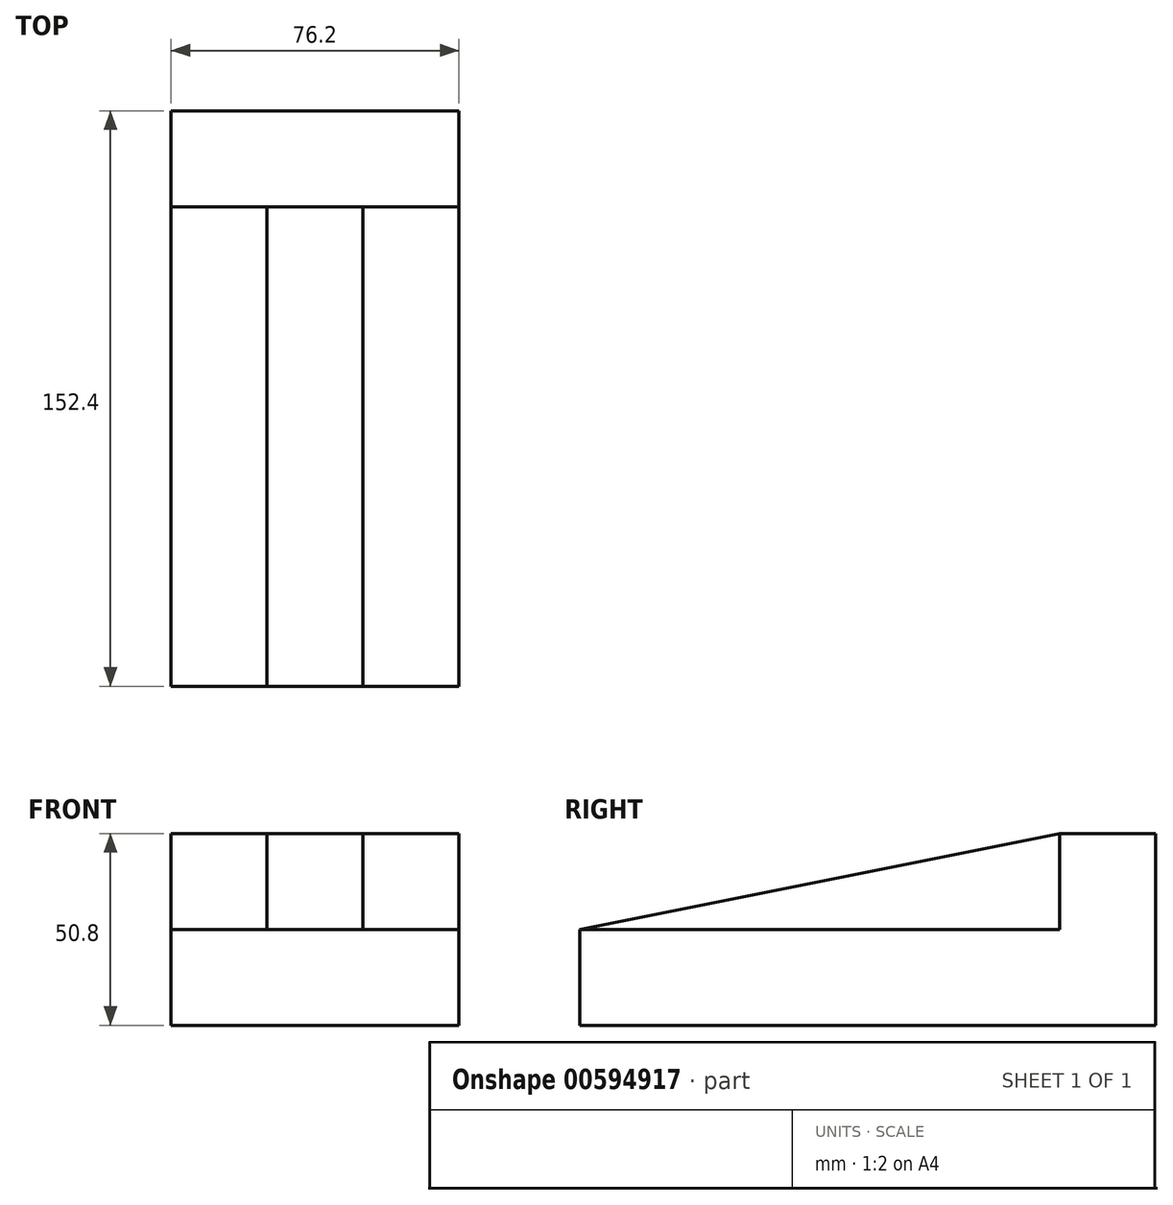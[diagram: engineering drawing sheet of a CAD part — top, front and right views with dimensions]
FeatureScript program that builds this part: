
annotation { "Feature Type Name" : "Feature", "Feature Type Description" : "" }
export const myFeature = defineFeature(function(context is Context, id is Id, definition is map)
    precondition{}
    {
        {
            var Q0;
            Q0=qCreatedBy(makeId("Right.planeOp"),FACE);
            var sketch = newSketch(context, id + "F0", { "sketchPlane" : qUnion([Q0])});
            skLineSegment(sketch, "E0", {"start": v(77.05, 20.16) * mm, "end": v(77.05, -30.64) * mm});
            skLineSegment(sketch, "E1", {"start": v(77.05, -30.64) * mm, "end": v(-75.35, -30.64) * mm});
            skLineSegment(sketch, "E2", {"start": v(-75.35, -30.64) * mm, "end": v(-75.35, -5.24) * mm});
            skLineSegment(sketch, "E3", {"start": v(-75.35, -5.24) * mm, "end": v(51.65, -5.24) * mm});
            skLineSegment(sketch, "E4", {"start": v(51.65, -5.24) * mm, "end": v(51.65, 20.16) * mm});
            skLineSegment(sketch, "E5", {"start": v(51.65, 20.16) * mm, "end": v(77.05, 20.16) * mm});
            skLineSegment(sketch, "E6", {"start": v(51.65, 20.16) * mm, "end": v(-75.35, -5.24) * mm});
            skSolve(sketch);
        }
        {
            var Q0;
            Q0=makeQuery(id+"F0.imprint","IMPRINT",FACE,{"disambiguationData":[TD([[makeQuery(id+"F0.imprint","IMPRINT",EDGE,{"derivedFrom":sQuery(id+"F0.wireOp",EDGE,"E3")}),1.0]])]});
            extrude(context, id + "F1", {"entities" : qUnion([Q0]), "depth" : 25.4 * mm, "offsetDistance" : 25.4 * mm});
        }
        {
            var Q0;
            Q0=makeQuery(id+"F0.imprint","IMPRINT",FACE,{"disambiguationData":[TD([[makeQuery(id+"F0.imprint","IMPRINT",EDGE,{"derivedFrom":sQuery(id+"F0.wireOp",EDGE,"E0")}),-1.0]])]});
            extrude(context, id + "F2", {"entities" : qUnion([Q0]), "operationType" : NewBodyOperationType.ADD, "depth" : 50.8 * mm, "offsetDistance" : 25.4 * mm, "hasSecondDirection" : true, "secondDirectionOppositeDirection" : true, "secondDirectionDepth" : 25.4 * mm});
        }
    });
